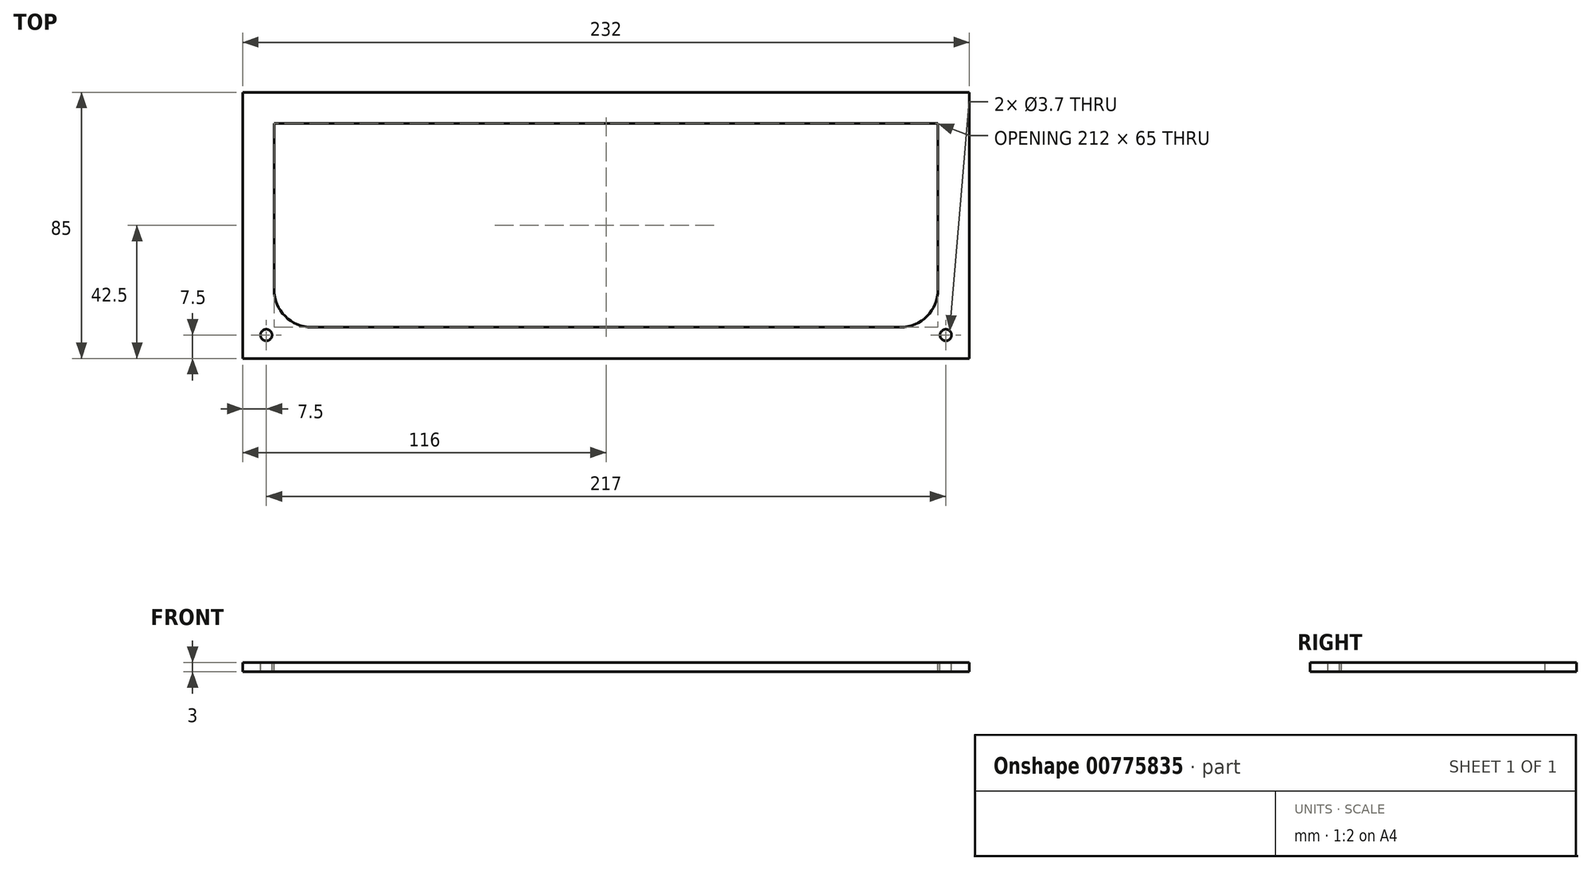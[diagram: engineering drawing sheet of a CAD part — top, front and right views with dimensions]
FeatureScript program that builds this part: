
annotation { "Feature Type Name" : "Feature", "Feature Type Description" : "" }
export const myFeature = defineFeature(function(context is Context, id is Id, definition is map)
    precondition{}
    {
        {
            var Q0;
            Q0=qCreatedBy(makeId("Top.planeOp"),FACE);
            var sketch = newSketch(context, id + "F0", { "sketchPlane" : qUnion([Q0])});
            skLineSegment(sketch, "E0.bottom", {"start": v(116, -42.5) * mm, "end": v(-116, -42.5) * mm});
            skLineSegment(sketch, "E0.top", {"start": v(116, 42.5) * mm, "end": v(-116, 42.5) * mm});
            skLineSegment(sketch, "E0.left", {"start": v(116, -42.5) * mm, "end": v(116, 42.5) * mm});
            skLineSegment(sketch, "E0.right", {"start": v(-116, -42.5) * mm, "end": v(-116, 42.5) * mm});
            skPoint(sketch, "E0.middle", {"position": v(0, 0) * mm});
            skSolve(sketch);
        }
        {
            assignVariable(context, id + "F1", {"name" : "thick", "anyValue" : 3 * mm});
        }
        {
            var Q0;
            Q0=makeQuery(id+"F0.imprint","IMPRINT",FACE,{"disambiguationData":[TD([[makeQuery(id+"F0.imprint","IMPRINT",EDGE,{"derivedFrom":sQuery(id+"F0.wireOp",EDGE,"E0.bottom")}),-1.0]])]});
            extrude(context, id + "F2", {"entities" : qUnion([Q0]), "depth" : getVariable(context, 'thick'), "offsetDistance" : 25 * mm});
        }
        {
            var Q0;
            Q0=makeQuery(id+"F2.opExtrude","CAP_FACE",FACE,{"disambiguationData":[OSD([sQuery(id+"F0.wireOp",EDGE,"E0.bottom"),sQuery(id+"F0.wireOp",EDGE,"E0.top"),sQuery(id+"F0.wireOp",EDGE,"E0.left"),sQuery(id+"F0.wireOp",EDGE,"E0.right")])],"isStart":false});
            var sketch = newSketch(context, id + "F3", { "sketchPlane" : qUnion([Q0])});
            skLineSegment(sketch, "E1.bottom", {"start": v(-116, 42.5) * mm, "end": v(-106, 42.5) * mm, "construction": true});
            skLineSegment(sketch, "E1.top", {"start": v(-116, 32.5) * mm, "end": v(-106, 32.5) * mm, "construction": true});
            skLineSegment(sketch, "E1.left", {"start": v(-116, 42.5) * mm, "end": v(-116, 32.5) * mm, "construction": true});
            skLineSegment(sketch, "E1.right", {"start": v(-106, 42.5) * mm, "end": v(-106, 32.5) * mm, "construction": true});
            skLineSegment(sketch, "E2.bottom", {"start": v(-106, 32.5) * mm, "end": v(106, 32.5) * mm});
            skLineSegment(sketch, "E2.top", {"start": v(-106, -32.5) * mm, "end": v(106, -32.5) * mm});
            skLineSegment(sketch, "E2.left", {"start": v(-106, 32.5) * mm, "end": v(-106, -32.5) * mm});
            skLineSegment(sketch, "E2.right", {"start": v(106, 32.5) * mm, "end": v(106, -32.5) * mm});
            skLineSegment(sketch, "E3.bottom", {"start": v(-116, -42.5) * mm, "end": v(-106, -42.5) * mm, "construction": true});
            skLineSegment(sketch, "E3.top", {"start": v(-116, -32.5) * mm, "end": v(-106, -32.5) * mm, "construction": true});
            skLineSegment(sketch, "E3.left", {"start": v(-116, -42.5) * mm, "end": v(-116, -32.5) * mm, "construction": true});
            skLineSegment(sketch, "E3.right", {"start": v(-106, -42.5) * mm, "end": v(-106, -32.5) * mm, "construction": true});
            skLineSegment(sketch, "E4.bottom", {"start": v(106, 32.5) * mm, "end": v(116, 32.5) * mm, "construction": true});
            skLineSegment(sketch, "E4.top", {"start": v(106, 42.5) * mm, "end": v(116, 42.5) * mm, "construction": true});
            skLineSegment(sketch, "E4.left", {"start": v(106, 32.5) * mm, "end": v(106, 42.5) * mm, "construction": true});
            skLineSegment(sketch, "E4.right", {"start": v(116, 32.5) * mm, "end": v(116, 42.5) * mm, "construction": true});
            skLineSegment(sketch, "E5.bottom", {"start": v(106, -32.5) * mm, "end": v(116, -32.5) * mm, "construction": true});
            skLineSegment(sketch, "E5.top", {"start": v(106, -42.5) * mm, "end": v(116, -42.5) * mm, "construction": true});
            skLineSegment(sketch, "E5.left", {"start": v(106, -32.5) * mm, "end": v(106, -42.5) * mm, "construction": true});
            skLineSegment(sketch, "E5.right", {"start": v(116, -32.5) * mm, "end": v(116, -42.5) * mm, "construction": true});
            skSolve(sketch);
        }
        {
            var Q0;
            Q0=makeQuery(id+"F3.imprint","IMPRINT",FACE,{"disambiguationData":[TD([[makeQuery(id+"F3.imprint","IMPRINT",EDGE,{"derivedFrom":sQuery(id+"F3.wireOp",EDGE,"E2.bottom")}),-1.0]])]});
            var Q1;
            Q1=makeQuery(id+"F3.imprint","IMPRINT",FACE,{"disambiguationData":[TD([[makeQuery(id+"F3.imprint","IMPRINT",EDGE,{"derivedFrom":sQuery(id+"F3.wireOp",EDGE,"q0CZnnEC-H3Zd-1A95-o37y-apkhwrDIlMcN.bottom")}),-1.0]])]});
            var Q2;
            Q2=makeQuery(id+"F3.imprint","IMPRINT",FACE,{"disambiguationData":[TD([[makeQuery(id+"F3.imprint","IMPRINT",EDGE,{"derivedFrom":sQuery(id+"F3.wireOp",EDGE,"NbjMPdAi-H4GH-f0D9-wTn7-TgyeDrorLurB.bottom")}),-1.0]])]});
            var Q3;
            Q3=makeQuery(id+"F3.imprint","IMPRINT",FACE,{"disambiguationData":[TD([[makeQuery(id+"F3.imprint","IMPRINT",EDGE,{"derivedFrom":sQuery(id+"F3.wireOp",EDGE,"sWnZ3NOe-Ncff-yfbY-mVAq-LZHHetCrOJVm.bottom")}),-1.0]])]});
            extrude(context, id + "F4", {"entities" : qUnion([Q0, Q1, Q2, Q3]), "operationType" : NewBodyOperationType.REMOVE, "oppositeDirection" : true, "depth" : getVariable(context, 'thick'), "offsetDistance" : 25 * mm});
        }
        {
            var Q0;
            Q0=makeQuery(id+"F4.boolean.opBoolean","COPY",EDGE,{"derivedFrom":makeQuery(id+"F4.opExtrude","SWEPT_EDGE",EDGE,{"disambiguationData":[OSD([sQuery(id+"F3.wireOp",EDGE,"E2.top"),sQuery(id+"F3.wireOp",EDGE,"E2.left")])]})});
            var Q1;
            Q1=makeQuery(id+"F4.boolean.opBoolean","COPY",EDGE,{"derivedFrom":makeQuery(id+"F4.opExtrude","SWEPT_EDGE",EDGE,{"disambiguationData":[OSD([sQuery(id+"F3.wireOp",EDGE,"E2.top"),sQuery(id+"F3.wireOp",EDGE,"E2.right")])]})});
            fillet(context, id + "F5", {"entities" : qUnion([Q0, Q1]), "radius" : 12 * mm, "tangentPropagation" : true, "allowEdgeOverflow" : false});
        }
        {
            var Q0;
            Q0=makeQuery(id+"F2.opExtrude","CAP_FACE",FACE,{"disambiguationData":[OSD([sQuery(id+"F0.wireOp",EDGE,"E0.bottom"),sQuery(id+"F0.wireOp",EDGE,"E0.top"),sQuery(id+"F0.wireOp",EDGE,"E0.left"),sQuery(id+"F0.wireOp",EDGE,"E0.right")])],"isStart":false});
            var sketch = newSketch(context, id + "F6", { "sketchPlane" : qUnion([Q0])});
            skLineSegment(sketch, "E6.bottom", {"start": v(-116, -42.5) * mm, "end": v(-108.5, -42.5) * mm, "construction": true});
            skLineSegment(sketch, "E6.top", {"start": v(-116, -35) * mm, "end": v(-108.5, -35) * mm, "construction": true});
            skLineSegment(sketch, "E6.left", {"start": v(-116, -42.5) * mm, "end": v(-116, -35) * mm, "construction": true});
            skLineSegment(sketch, "E6.right", {"start": v(-108.5, -42.5) * mm, "end": v(-108.5, -35) * mm, "construction": true});
            skLineSegment(sketch, "E7.bottom", {"start": v(116, -42.5) * mm, "end": v(108.5, -42.5) * mm, "construction": true});
            skLineSegment(sketch, "E7.top", {"start": v(116, -35) * mm, "end": v(108.5, -35) * mm, "construction": true});
            skLineSegment(sketch, "E7.left", {"start": v(116, -42.5) * mm, "end": v(116, -35) * mm, "construction": true});
            skLineSegment(sketch, "E7.right", {"start": v(108.5, -42.5) * mm, "end": v(108.5, -35) * mm, "construction": true});
            skCircle(sketch, "E8", {"center": v(-108.5, -35) * mm, "radius": 1.85 * mm});
            skCircle(sketch, "E9", {"center": v(108.5, -35) * mm, "radius": 1.85 * mm});
            skSolve(sketch);
        }
        {
            var Q0;
            Q0=qSketchRegion(id+"F6",true);
            extrude(context, id + "F7", {"entities" : qUnion([Q0]), "operationType" : NewBodyOperationType.REMOVE, "oppositeDirection" : true, "depth" : getVariable(context, 'thick'), "offsetDistance" : 25 * mm});
        }
    });
